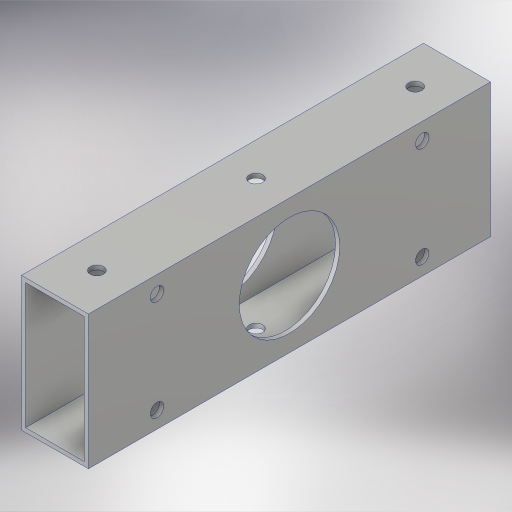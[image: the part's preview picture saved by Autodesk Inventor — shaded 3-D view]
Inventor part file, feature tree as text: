
AUTODESK INVENTOR PART (.ipt)
format: ipt  version: 2023.4 (Build 274418000, 418)  size: 313,856 bytes
history: native  units: in
note: dims shown in document units (in); Inventor stores cm internally (conversion verified against a paired STEP export)
features: sketch x4, hole x3, extrude x2, projected_geometry x1
ambient origin geometry x8: Origin, YZ Plane, XZ Plane, XY Plane, X Axis, Y Axis, Z Axis, Center Point
bodies: Solid1 (feature_tree)
feature tree (10):
  extrude  "Extrusion1"  Depth=4.75in
  hole  "Hole1"  [1 undecoded]
  hole  "Hole3"  [1 undecoded]
  extrude  "Extrusion2"  Depth=1.0in
  hole  "Hole2"  [1 undecoded]
  sketch  "Sketch2"  dims[d4=0.0in d5=4.75in]
  projected_geometry  "Projected Loop1"
  sketch  "Sketch3"  dims[d6=0.201in d7=0.75in d8=0.385in d9=0.25in d10=0.5635in d11=1.0in d12=0.8108in d14=4.7244in]
  sketch  "Sketch4"  dims[d15=3.7402in d16=4.2323in]
  sketch  "Sketch5"  dims[d17=1.5in d18=0.156in d19=0.38in d20=0.375in d21=0.25in d22=0.5635in d23=1.0in d24=0.8108in d25=4.2323in d28=1.5in d29=0.201in d30=0.38in d31=0.385in d32=0.25in d33=0.5635in d34=1.0in d35=0.8108in d36=1.5in d37=1.0in d38=0.0in]
note: 3 required parameter values undecoded (feature->parameter linkage not recoverable at this tier; creation-order binding heuristic only, values carry confidence <= 0.55)
